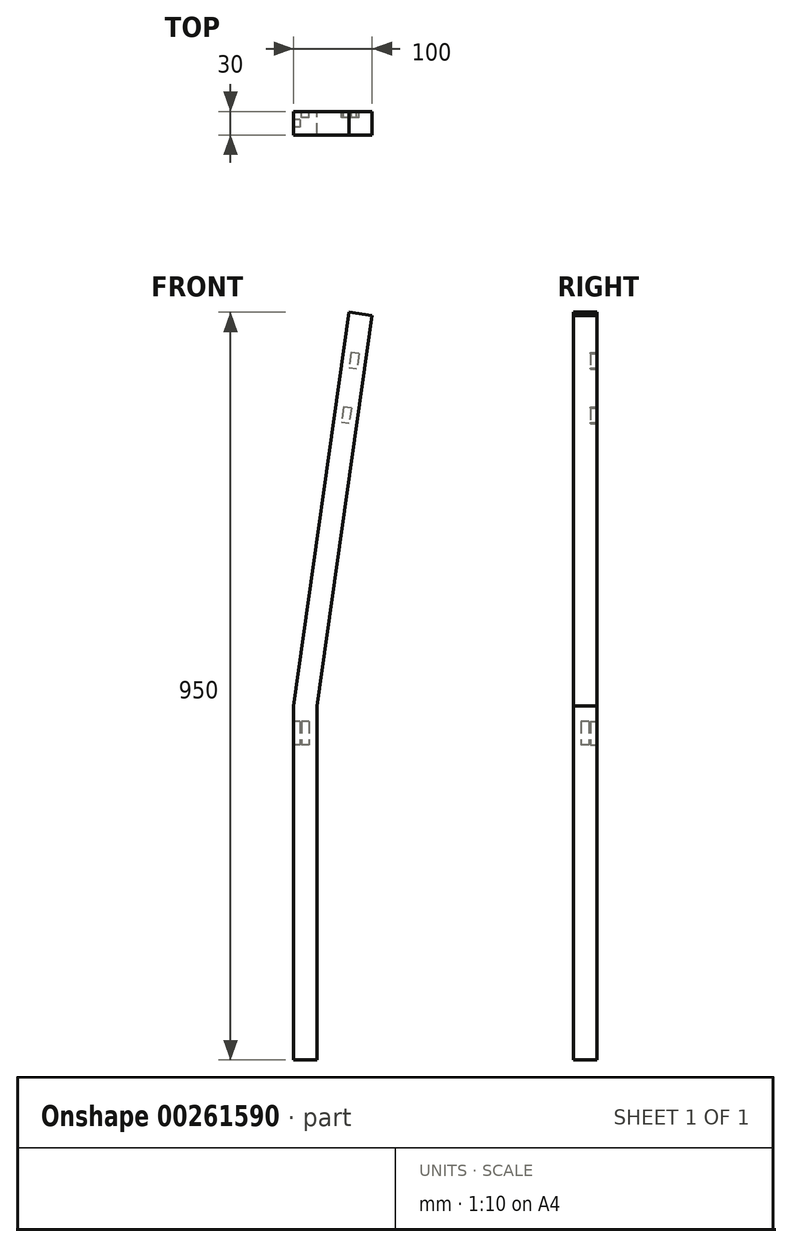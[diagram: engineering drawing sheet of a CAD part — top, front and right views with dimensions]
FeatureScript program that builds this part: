
annotation { "Feature Type Name" : "Feature", "Feature Type Description" : "" }
export const myFeature = defineFeature(function(context is Context, id is Id, definition is map)
    precondition{}
    {
        {
            var Q0;
            Q0=qCreatedBy(makeId("Front.planeOp"),FACE);
            var sketch = newSketch(context, id + "F0", { "sketchPlane" : qUnion([Q0])});
            skLineSegment(sketch, "E0", {"start": v(0, 0) * mm, "end": v(0, -450) * mm});
            skLineSegment(sketch, "E1", {"start": v(0, -450) * mm, "end": v(30, -450) * mm});
            skLineSegment(sketch, "E2", {"start": v(30, -450) * mm, "end": v(30, 0) * mm});
            skLineSegment(sketch, "E3", {"start": v(30, 0) * mm, "end": v(100, 495.8) * mm});
            skLineSegment(sketch, "E4", {"start": v(100, 495.8) * mm, "end": v(70.3, 500) * mm});
            skLineSegment(sketch, "E5", {"start": v(70.3, 500) * mm, "end": v(0, 0) * mm});
            skSolve(sketch);
        }
        {
            var Q0;
            Q0 = qSketchRegion(id + "F0", true);
            extrude(context, id + "F1", {"entities" : qUnion([Q0]), "depth" : 30 * mm});
        }
        {
            var Q0;
            Q0=makeQuery(id+"F1.opExtrude","CAP_FACE",FACE,{"disambiguationData":[OSD([sQuery(id+"F0.wireOp",EDGE,"E0"),sQuery(id+"F0.wireOp",EDGE,"E1"),sQuery(id+"F0.wireOp",EDGE,"E2"),sQuery(id+"F0.wireOp",EDGE,"E3"),sQuery(id+"F0.wireOp",EDGE,"E4"),sQuery(id+"F0.wireOp",EDGE,"E5")])],"isStart":true});
            var sketch = newSketch(context, id + "F2", { "sketchPlane" : qUnion([Q0])});
            skLineSegment(sketch, "E6.bottom", {"start": v(-83.14, 447.7) * mm, "end": v(-73.23, 449.09) * mm});
            skLineSegment(sketch, "E6.top", {"start": v(-80.35, 427.89) * mm, "end": v(-70.45, 429.28) * mm});
            skLineSegment(sketch, "E6.left", {"start": v(-83.14, 447.7) * mm, "end": v(-80.35, 427.89) * mm});
            skLineSegment(sketch, "E6.right", {"start": v(-73.23, 449.09) * mm, "end": v(-70.45, 429.28) * mm});
            skLineSegment(sketch, "E7.bottom", {"start": v(-73.4, 378.38) * mm, "end": v(-63.49, 379.77) * mm});
            skLineSegment(sketch, "E7.top", {"start": v(-70.6, 358.57) * mm, "end": v(-60.7, 359.96) * mm});
            skLineSegment(sketch, "E7.left", {"start": v(-73.4, 378.38) * mm, "end": v(-70.6, 358.57) * mm});
            skLineSegment(sketch, "E7.right", {"start": v(-63.49, 379.77) * mm, "end": v(-60.7, 359.96) * mm});
            skSolve(sketch);
        }
        {
            var Q0;
            Q0 = qSketchRegion(id + "F2", true);
            extrude(context, id + "F3", {"entities" : qUnion([Q0]), "operationType" : NewBodyOperationType.REMOVE, "oppositeDirection" : true, "depth" : 8 * mm});
        }
        {
            var Q0;
            Q0=makeQuery(id+"F1.opExtrude","CAP_FACE",FACE,{"disambiguationData":[OSD([sQuery(id+"F0.wireOp",EDGE,"E0"),sQuery(id+"F0.wireOp",EDGE,"E1"),sQuery(id+"F0.wireOp",EDGE,"E2"),sQuery(id+"F0.wireOp",EDGE,"E3"),sQuery(id+"F0.wireOp",EDGE,"E4"),sQuery(id+"F0.wireOp",EDGE,"E5")])],"isStart":true});
            var sketch = newSketch(context, id + "F4", { "sketchPlane" : qUnion([Q0])});
            skLineSegment(sketch, "E8.bottom", {"start": v(-20, -20) * mm, "end": v(-10, -20) * mm});
            skLineSegment(sketch, "E8.top", {"start": v(-20, -50) * mm, "end": v(-10, -50) * mm});
            skLineSegment(sketch, "E8.left", {"start": v(-20, -20) * mm, "end": v(-20, -50) * mm});
            skLineSegment(sketch, "E8.right", {"start": v(-10, -20) * mm, "end": v(-10, -50) * mm});
            skSolve(sketch);
        }
        {
            var Q0;
            Q0 = qSketchRegion(id + "F4", true);
            extrude(context, id + "F5", {"entities" : qUnion([Q0]), "operationType" : NewBodyOperationType.REMOVE, "oppositeDirection" : true, "depth" : 8 * mm});
        }
        {
            var Q0;
            Q0=makeQuery(id+"F1.opExtrude","SWEPT_FACE",FACE,{"disambiguationData":[OSD([sQuery(id+"F0.wireOp",EDGE,"E0")])]});
            var sketch = newSketch(context, id + "F6", { "sketchPlane" : qUnion([Q0])});
            skLineSegment(sketch, "E9.bottom", {"start": v(10, -20) * mm, "end": v(20, -20) * mm});
            skLineSegment(sketch, "E9.top", {"start": v(10, -50) * mm, "end": v(20, -50) * mm});
            skLineSegment(sketch, "E9.left", {"start": v(10, -20) * mm, "end": v(10, -50) * mm});
            skLineSegment(sketch, "E9.right", {"start": v(20, -20) * mm, "end": v(20, -50) * mm});
            skSolve(sketch);
        }
        {
            var Q0;
            Q0 = qSketchRegion(id + "F6", true);
            extrude(context, id + "F7", {"entities" : qUnion([Q0]), "operationType" : NewBodyOperationType.REMOVE, "oppositeDirection" : true, "depth" : 8 * mm});
        }
    });
